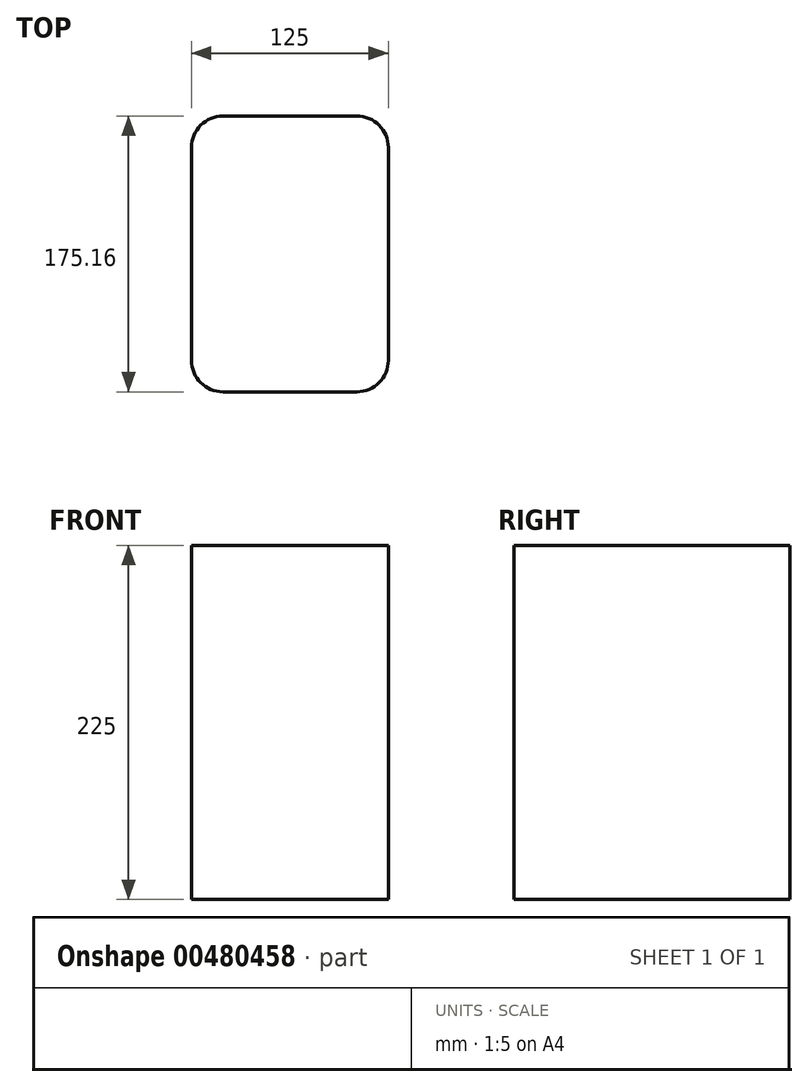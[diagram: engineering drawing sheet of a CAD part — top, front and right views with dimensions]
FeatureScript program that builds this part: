
annotation { "Feature Type Name" : "Feature", "Feature Type Description" : "" }
export const myFeature = defineFeature(function(context is Context, id is Id, definition is map)
    precondition{}
    {
        {
            var Q0;
            Q0=qCreatedBy(makeId("Top.planeOp"),FACE);
            var sketch = newSketch(context, id + "F0", { "sketchPlane" : qUnion([Q0])});
            skLineSegment(sketch, "E0", {"start": v(-116, 95.54) * mm, "end": v(-31, 95.54) * mm});
            skLineSegment(sketch, "E1", {"start": v(-11, 75.54) * mm, "end": v(-11, -59.62) * mm});
            skLineSegment(sketch, "E2", {"start": v(-31, -79.62) * mm, "end": v(-116, -79.62) * mm});
            skPoint(sketch, "E3.visualSharp", {"position": v(-11, 95.54) * mm});
            skArc(sketch, "E3.filletArc", {"start": v(-11, 75.54) * mm, "mid": v(-16.86, 89.69) * mm, "end": v(-31, 95.54) * mm});
            skPoint(sketch, "E4.visualSharp", {"position": v(-11, -79.62) * mm});
            skArc(sketch, "E4.filletArc", {"start": v(-31, -79.62) * mm, "mid": v(-16.86, -73.76) * mm, "end": v(-11, -59.62) * mm});
            skLineSegment(sketch, "E5", {"start": v(-136, -59.62) * mm, "end": v(-136, 75.54) * mm});
            skArc(sketch, "E6.filletArc", {"start": v(-116, 95.54) * mm, "mid": v(-130.14, 89.69) * mm, "end": v(-136, 75.54) * mm});
            skPoint(sketch, "E7.visualSharp", {"position": v(-136, -79.62) * mm});
            skArc(sketch, "E7.filletArc", {"start": v(-136, -59.62) * mm, "mid": v(-130.14, -73.76) * mm, "end": v(-116, -79.62) * mm});
            skSolve(sketch);
        }
        {
            var Q0;
            Q0 = qSketchRegion(id + "F0", true);
            extrude(context, id + "F1", {"entities" : qUnion([Q0]), "depth" : 225 * mm});
        }
    });
